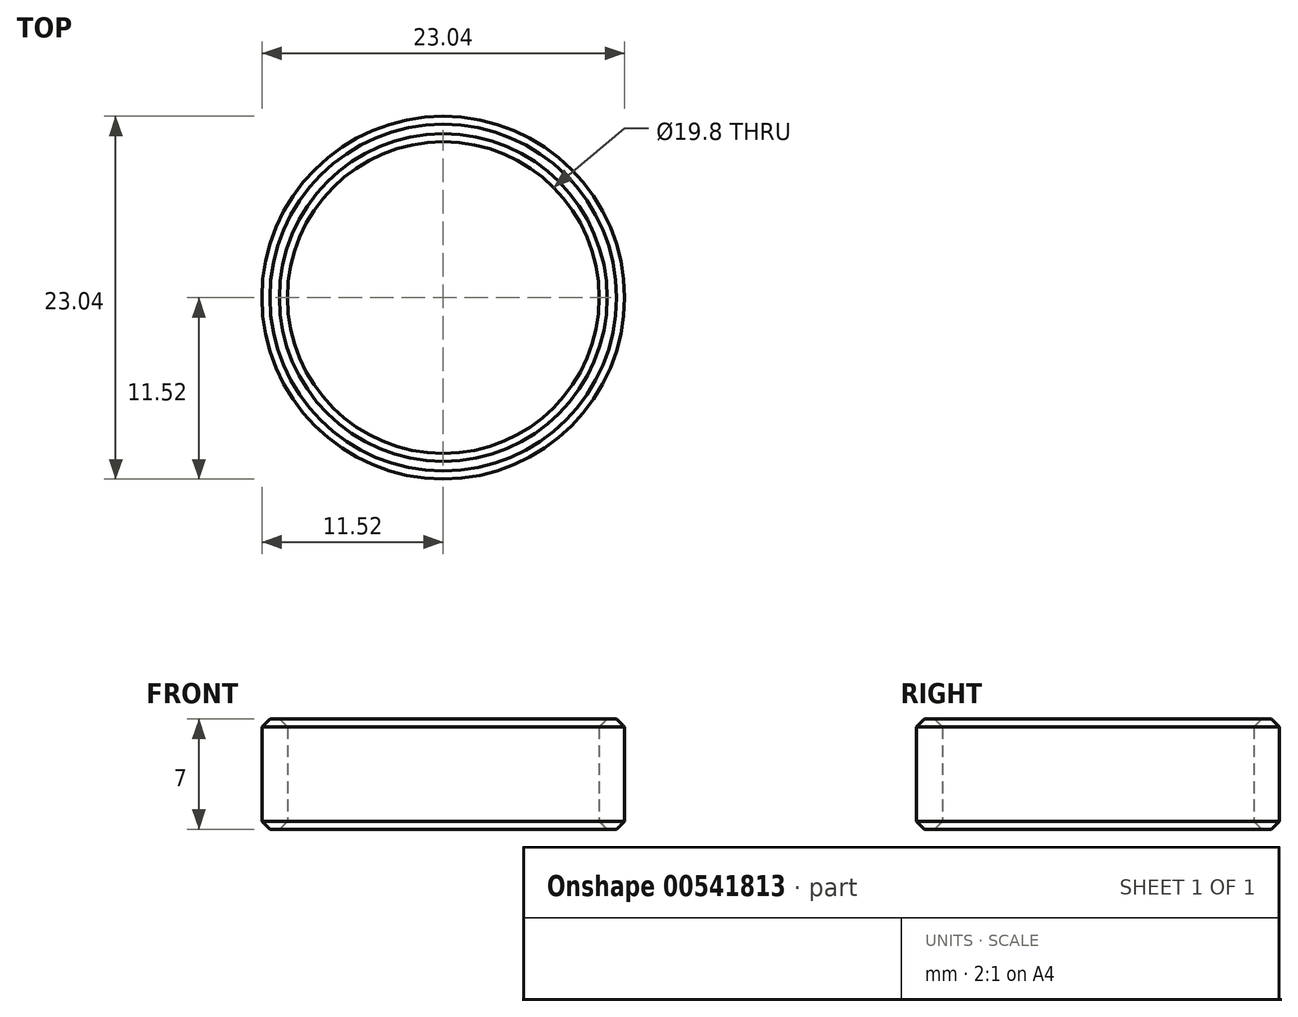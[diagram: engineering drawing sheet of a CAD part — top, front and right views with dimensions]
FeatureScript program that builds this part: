
annotation { "Feature Type Name" : "Feature", "Feature Type Description" : "" }
export const myFeature = defineFeature(function(context is Context, id is Id, definition is map)
    precondition{}
    {
        {
            var Q0;
            Q0=qCreatedBy(makeId("Top.planeOp"),FACE);
            var sketch = newSketch(context, id + "F0", { "sketchPlane" : qUnion([Q0])});
            skCircle(sketch, "E0", {"center": v(0, 0) * mm, "radius": 9.9 * mm});
            skCircle(sketch, "E1", {"center": v(0, 0) * mm, "radius": 11.52 * mm});
            skSolve(sketch);
        }
        {
            var Q0;
            Q0=makeQuery(id+"F0.imprint","IMPRINT",FACE,{"disambiguationData":[TD([[makeQuery(id+"F0.imprint","IMPRINT",EDGE,{"derivedFrom":sQuery(id+"F0.wireOp",EDGE,"E0")}),-1.0]])]});
            extrude(context, id + "F1", {"entities" : qUnion([Q0]), "depth" : 7 * mm, "offsetDistance" : 25.4 * mm});
        }
        {
            var Q0;
            Q0=makeQuery(id+"F1.opExtrude","CAP_EDGE",EDGE,{"disambiguationData":[OSD([sQuery(id+"F0.wireOp",EDGE,"E0")])],"isStart":true});
            var Q1;
            Q1=makeQuery(id+"F1.opExtrude","CAP_EDGE",EDGE,{"disambiguationData":[OSD([sQuery(id+"F0.wireOp",EDGE,"E0")])],"isStart":false});
            chamfer(context, id + "F2", {"entities" : qUnion([Q0, Q1]), "width" : 0.5 * mm, "tangentPropagation" : true});
        }
        {
            var Q0;
            Q0=makeQuery(id+"F1.opExtrude","CAP_EDGE",EDGE,{"disambiguationData":[OSD([sQuery(id+"F0.wireOp",EDGE,"E1")])],"isStart":false});
            var Q1;
            Q1=makeQuery(id+"F1.opExtrude","CAP_EDGE",EDGE,{"disambiguationData":[OSD([sQuery(id+"F0.wireOp",EDGE,"E1")])],"isStart":true});
            chamfer(context, id + "F3", {"entities" : qUnion([Q0, Q1]), "width" : 0.5 * mm, "tangentPropagation" : true});
        }
    });
